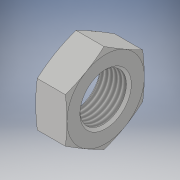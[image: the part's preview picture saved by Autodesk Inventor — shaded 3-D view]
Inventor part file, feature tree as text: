
AUTODESK INVENTOR PART (.ipt)
format: ipt  version: 2019 (Build 230136000, 136)  size: 165,888 bytes
history: native  units: mm
features: other x21, sketch x3, revolve x2, extrude x1, thread x1
ambient origin geometry x8: Origin, YZ Plane, XZ Plane, XY Plane, X Axis, Y Axis, Z Axis, Center Point
bodies: Solid1 (feature_tree)
feature tree (28):
  revolve  "Revolution1"  [1 undecoded]
  extrude  "Extrusion1"  Depth=8.12546mm TaperAngle=0.0deg
  revolve  "Revolution2"  [1 undecoded]
  thread  "Thread1"  [1 undecoded]
  other  "c_XY"
  other  "c_YZ"
  other  "c_ZX"
  other  "c_X"
  other  "c_Y"
  other  "c_Z"
  other  "c_Center"
  other  "kb_XY"
  other  "kb_YZ"
  other  "kb_ZX"
  other  "kb_X"
  other  "kb_Y"
  other  "kb_Z"
  other  "kb_Center"
  other  "nut_XY"
  other  "nut_YZ"
  other  "nut_ZX"
  other  "nut_X"
  other  "nut_Y"
  other  "nut_Z"
  other  "nut_Center"
  sketch  "Sketch_1"  dims[d0=360.0deg d1=9.652mm d2=0.0mm]
  sketch  "Sketch_2"  dims[d3=360.0deg d4=8.12546mm d5=0.0mm]
  sketch  "Sketch_3"  dims[d6=0.0mm d7=0.0mm]
note: 3 required parameter values undecoded (feature->parameter linkage not recoverable at this tier; creation-order binding heuristic only, values carry confidence <= 0.55)